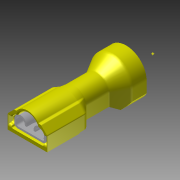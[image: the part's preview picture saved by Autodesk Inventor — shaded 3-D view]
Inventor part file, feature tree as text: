
AUTODESK INVENTOR PART (.ipt)
format: ipt  version: 2011 (Build 150239000, 239)  size: 908,800 bytes
history: native  units: mm
features: other x4, plane x2, imported_body x1, sketch x1
ambient origin geometry x8: Origin, YZ Plane, XZ Plane, XY Plane, X Axis, Y Axis, Z Axis, Center Point
bodies: Solid1 (feature_tree)
feature tree (8):
  imported_body  "Base1"
  sketch  "Sketch1"  dims[d0=3.175mm d1=6.35mm]
  other  "Work Point2"
  other  "Work Point3"
  plane  "Work Plane1"
  other  "Work Axis1"
  plane  "Work Plane2"
  other  "Work Axis2"
